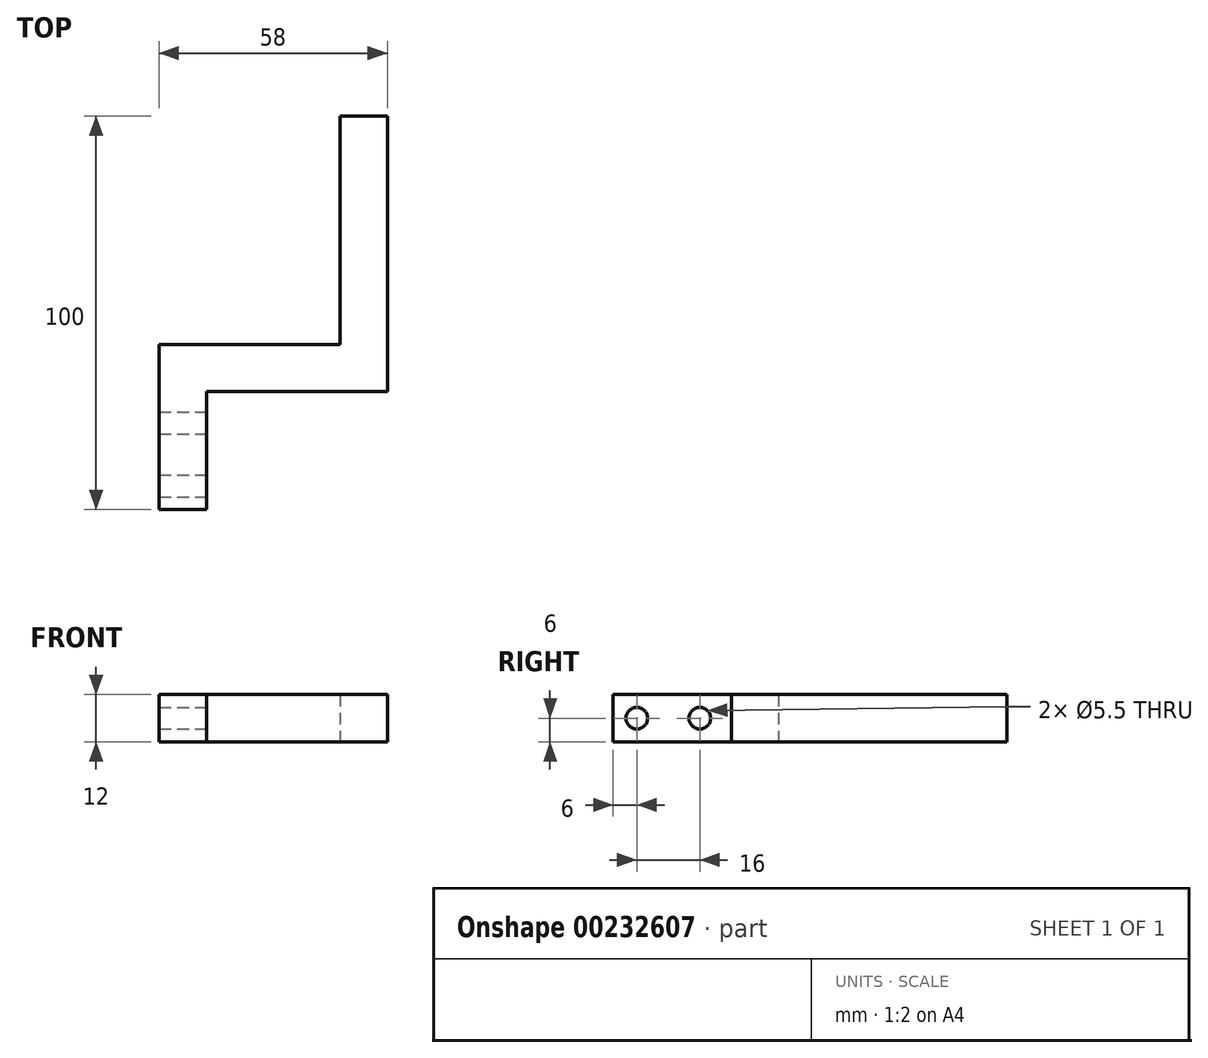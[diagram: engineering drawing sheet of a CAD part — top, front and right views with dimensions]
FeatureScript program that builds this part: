
annotation { "Feature Type Name" : "Feature", "Feature Type Description" : "" }
export const myFeature = defineFeature(function(context is Context, id is Id, definition is map)
    precondition{}
    {
        {
            var Q0;
            Q0=qCreatedBy(makeId("Top.planeOp"),FACE);
            var sketch = newSketch(context, id + "F0", { "sketchPlane" : qUnion([Q0])});
            skLineSegment(sketch, "E0", {"start": v(0, 0) * mm, "end": v(0, -30) * mm});
            skLineSegment(sketch, "E1", {"start": v(0, -30) * mm, "end": v(12, -30) * mm});
            skLineSegment(sketch, "E2", {"start": v(12, -30) * mm, "end": v(12, 0) * mm});
            skLineSegment(sketch, "E3", {"start": v(12, 0) * mm, "end": v(58, 0) * mm});
            skLineSegment(sketch, "E4", {"start": v(58, 0) * mm, "end": v(58, 70) * mm});
            skLineSegment(sketch, "E5", {"start": v(58, 70) * mm, "end": v(46, 70) * mm});
            skLineSegment(sketch, "E6", {"start": v(46, 70) * mm, "end": v(46, 12) * mm});
            skLineSegment(sketch, "E7", {"start": v(46, 12) * mm, "end": v(0, 12) * mm});
            skLineSegment(sketch, "E8", {"start": v(0, 12) * mm, "end": v(0, 0) * mm});
            skSolve(sketch);
        }
        {
            var Q0;
            Q0 = qSketchRegion(id + "F0", true);
            extrude(context, id + "F1", {"entities" : qUnion([Q0]), "depth" : 12 * mm});
        }
        {
            var Q0;
            Q0=makeQuery(id+"F1.opExtrude","SWEPT_FACE",FACE,{"disambiguationData":[OSD([sQuery(id+"F0.wireOp",EDGE,"E2")])]});
            var sketch = newSketch(context, id + "F2", { "sketchPlane" : qUnion([Q0])});
            skCircle(sketch, "E9", {"center": v(-24, 6) * mm, "radius": 2.75 * mm});
            skCircle(sketch, "E10", {"center": v(-8, 6) * mm, "radius": 2.75 * mm});
            skSolve(sketch);
        }
        {
            var Q0;
            Q0 = qSketchRegion(id + "F2", true);
            extrude(context, id + "F3", {"entities" : qUnion([Q0]), "operationType" : NewBodyOperationType.REMOVE, "endBound" : BoundingType.THROUGH_ALL, "oppositeDirection" : true, "depth" : 25 * mm});
        }
    });
